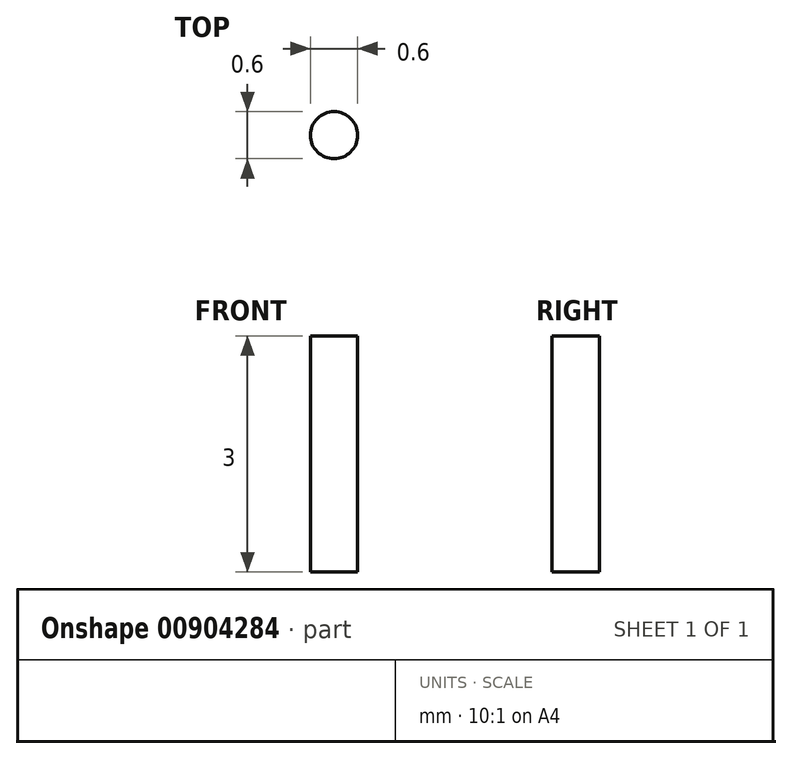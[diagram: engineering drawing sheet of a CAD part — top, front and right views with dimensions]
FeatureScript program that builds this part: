
annotation { "Feature Type Name" : "Feature", "Feature Type Description" : "" }
export const myFeature = defineFeature(function(context is Context, id is Id, definition is map)
    precondition{}
    {
        {
            var Q0;
            Q0=qCreatedBy(makeId("Front.planeOp"),FACE);
            var sketch = newSketch(context, id + "F0", { "sketchPlane" : qUnion([Q0])});
            skLineSegment(sketch, "E0.bottom", {"start": v(0, 0) * mm, "end": v(-0.3, 0) * mm});
            skLineSegment(sketch, "E0.top", {"start": v(0, 3) * mm, "end": v(-0.3, 3) * mm});
            skLineSegment(sketch, "E0.left", {"start": v(0, 0) * mm, "end": v(0, 3) * mm});
            skLineSegment(sketch, "E0.right", {"start": v(-0.3, 0) * mm, "end": v(-0.3, 3) * mm});
            skSolve(sketch);
        }
        {
            var Q0;
            Q0=makeQuery(id+"F0.imprint","IMPRINT",FACE,{"disambiguationData":[TD([[makeQuery(id+"F0.imprint","IMPRINT",EDGE,{"derivedFrom":sQuery(id+"F0.wireOp",EDGE,"E0.bottom")}),-1.0]])]});
            var Q1;
            Q1=sQuery(id+"F0.wireOp",EDGE,"E0.left");
            revolve(context, id + "F1", {"surfaceOperationType" : NewSurfaceOperationType.NEW, "entities" : qUnion([Q0]), "axis" : qUnion([Q1]), "revolveType" : RevolveType.FULL});
        }
    });
